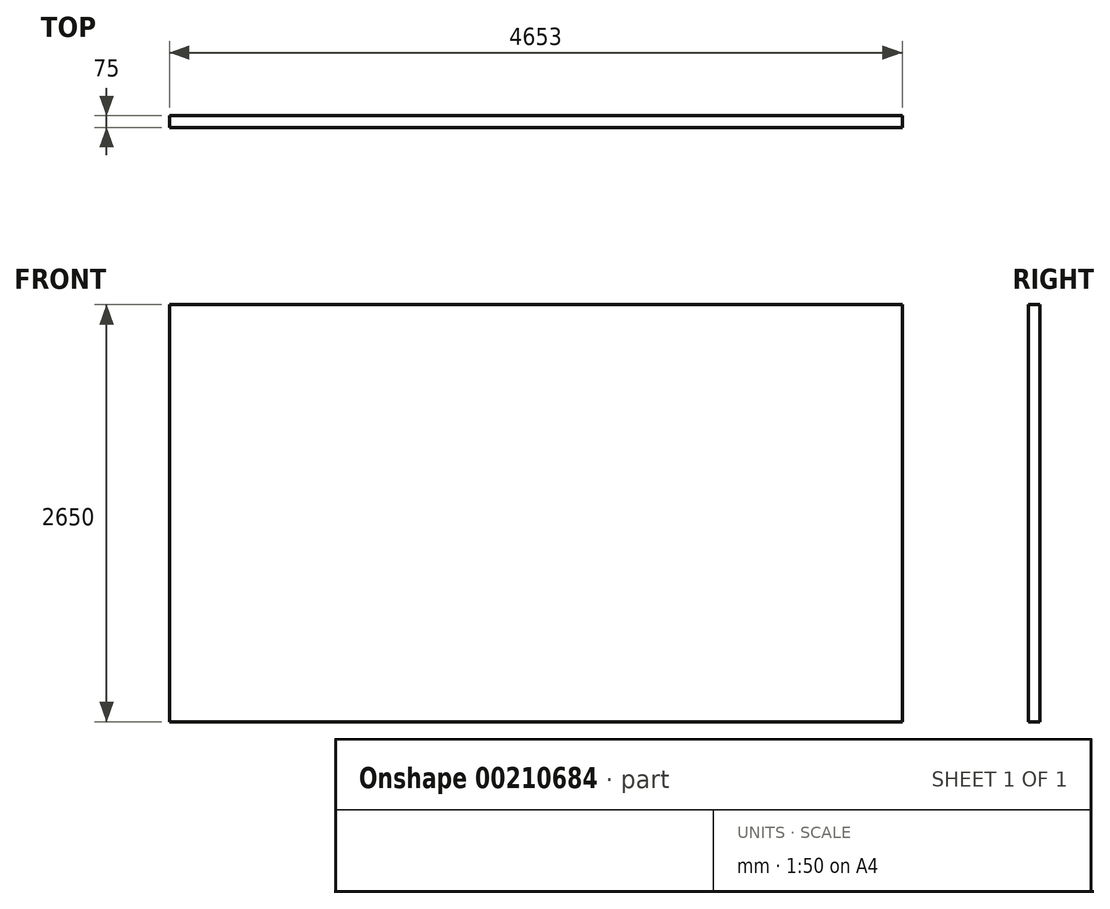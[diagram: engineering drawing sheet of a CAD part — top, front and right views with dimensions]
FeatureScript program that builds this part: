
annotation { "Feature Type Name" : "Feature", "Feature Type Description" : "" }
export const myFeature = defineFeature(function(context is Context, id is Id, definition is map)
    precondition{}
    {
        {
            var Q0;
            Q0=qCreatedBy(makeId("Front.planeOp"),FACE);
            var sketch = newSketch(context, id + "F0", { "sketchPlane" : qUnion([Q0])});
            skLineSegment(sketch, "E0.bottom", {"start": v(0, 0) * mm, "end": v(4653, 0) * mm});
            skLineSegment(sketch, "E0.left", {"start": v(0, 0) * mm, "end": v(0, 2650) * mm});
            skLineSegment(sketch, "E0.right", {"start": v(4653, 0) * mm, "end": v(4653, 2650) * mm});
            skLineSegment(sketch, "E1", {"start": v(0, 2650) * mm, "end": v(4653, 2650) * mm});
            skSolve(sketch);
        }
        {
            var Q0;
            Q0=makeQuery(id+"F0.imprint","IMPRINT",FACE,{"disambiguationData":[TD([[makeQuery(id+"F0.imprint","IMPRINT",EDGE,{"derivedFrom":sQuery(id+"F0.wireOp",EDGE,"E0.bottom")}),1.0]])]});
            extrude(context, id + "F1", {"entities" : qUnion([Q0]), "depth" : 75 * mm});
        }
    });
